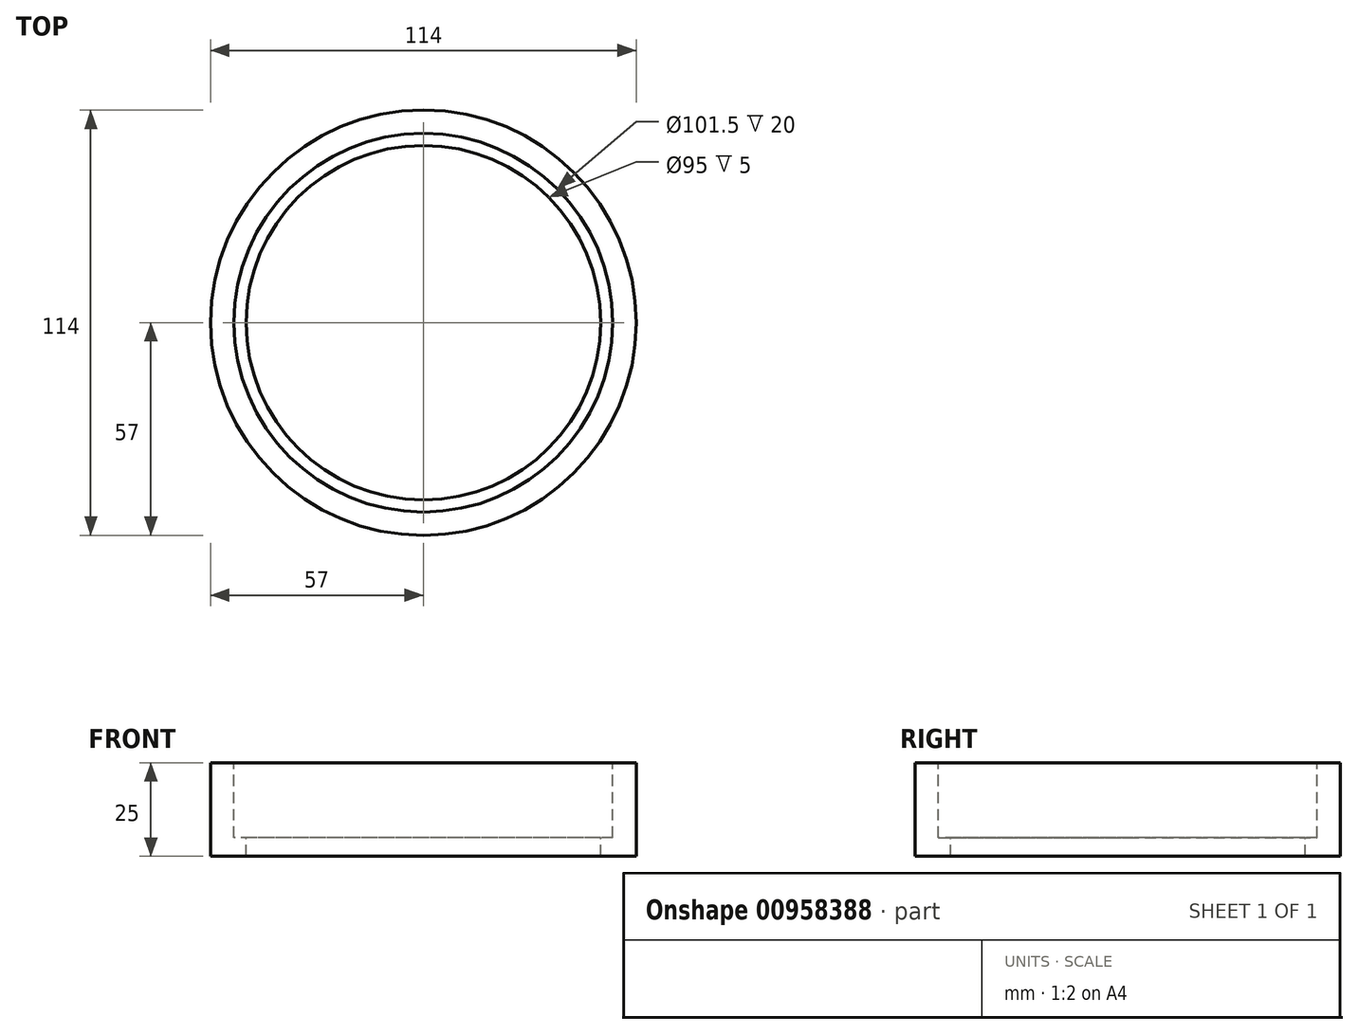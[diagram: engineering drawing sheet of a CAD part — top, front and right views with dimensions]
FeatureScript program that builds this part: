
annotation { "Feature Type Name" : "Feature", "Feature Type Description" : "" }
export const myFeature = defineFeature(function(context is Context, id is Id, definition is map)
    precondition{}
    {
        {
            var Q0;
            Q0=qCreatedBy(makeId("Front.planeOp"),FACE);
            var sketch = newSketch(context, id + "F0", { "sketchPlane" : qUnion([Q0])});
            skLineSegment(sketch, "E0", {"start": v(57, 0) * mm, "end": v(57, 25) * mm});
            skLineSegment(sketch, "E1", {"start": v(57, 0) * mm, "end": v(47.5, 0) * mm});
            skLineSegment(sketch, "E2", {"start": v(47.5, 0) * mm, "end": v(47.5, 5) * mm});
            skLineSegment(sketch, "E3", {"start": v(57, 25) * mm, "end": v(50.75, 25) * mm});
            skLineSegment(sketch, "E4", {"start": v(50.75, 25) * mm, "end": v(50.75, 5) * mm});
            skLineSegment(sketch, "E5", {"start": v(50.75, 5) * mm, "end": v(47.5, 5) * mm});
            skLineSegment(sketch, "E6", {"start": v(0, 61.9) * mm, "end": v(0, -70.2) * mm, "construction": true});
            skSolve(sketch);
        }
        {
            var Q0;
            Q0=qSketchRegion(id+"F0",true);
            var Q1;
            Q1=sQuery(id+"F0.wireOp",EDGE,"E6");
            revolve(context, id + "F1", {"surfaceOperationType" : NewSurfaceOperationType.NEW, "entities" : qUnion([Q0]), "axis" : qUnion([Q1]), "revolveType" : RevolveType.FULL});
        }
    });
